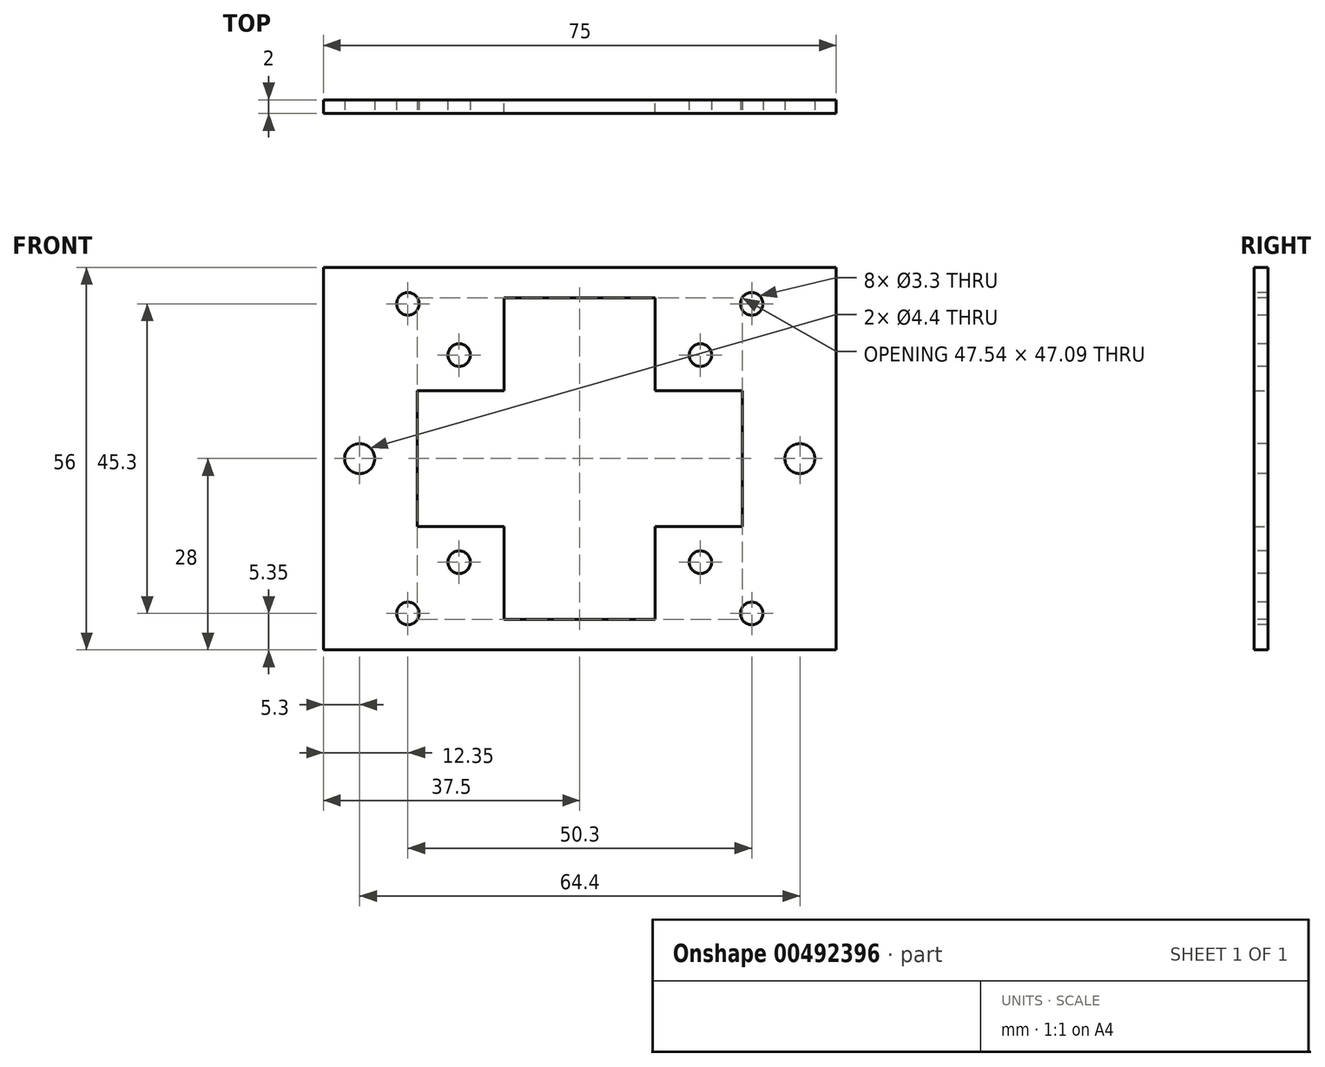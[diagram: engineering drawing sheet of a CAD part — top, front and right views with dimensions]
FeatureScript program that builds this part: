
annotation { "Feature Type Name" : "Feature", "Feature Type Description" : "" }
export const myFeature = defineFeature(function(context is Context, id is Id, definition is map)
    precondition{}
    {
        {
            var Q0;
            Q0=qCreatedBy(makeId("Front.planeOp"),FACE);
            var sketch = newSketch(context, id + "F0", { "sketchPlane" : qUnion([Q0])});
            skLineSegment(sketch, "E0.bottom", {"start": v(-37.5, 28) * mm, "end": v(37.5, 28) * mm});
            skLineSegment(sketch, "E0.top", {"start": v(-37.5, -28) * mm, "end": v(37.5, -28) * mm});
            skLineSegment(sketch, "E0.left", {"start": v(-37.5, 28) * mm, "end": v(-37.5, -28) * mm});
            skLineSegment(sketch, "E0.right", {"start": v(37.5, 28) * mm, "end": v(37.5, -28) * mm});
            skSolve(sketch);
        }
        {
            var Q0;
            Q0 = qSketchRegion(id + "F0", true);
            extrude(context, id + "F1", {"entities" : qUnion([Q0]), "depth" : 2 * mm, "offsetDistance" : 25 * mm});
        }
        {
            var Q0;
            Q0=makeQuery(id+"F1.opExtrude","CAP_FACE",FACE,{"disambiguationData":[OSD([sQuery(id+"F0.wireOp",EDGE,"E0.bottom"),sQuery(id+"F0.wireOp",EDGE,"E0.top"),sQuery(id+"F0.wireOp",EDGE,"E0.left"),sQuery(id+"F0.wireOp",EDGE,"E0.right")])],"isStart":false});
            var sketch = newSketch(context, id + "F2", { "sketchPlane" : qUnion([Q0])});
            skPoint(sketch, "E1", {"position": v(-32.2, 0) * mm});
            skPoint(sketch, "E2", {"position": v(32.2, 0) * mm});
            skSolve(sketch);
        }
        {
            var Q0;
            Q0=sQuery(id+"F2.wireOp",VERTEX,"E1");
            var Q1;
            Q1=sQuery(id+"F2.wireOp",VERTEX,"E2");
            var Q2;
            Q2=makeQuery(id+"F1.opExtrude","SWEPT_BODY",BODY,{"disambiguationData":[OSD([sQuery(id+"F0.wireOp",EDGE,"E0.bottom"),sQuery(id+"F0.wireOp",EDGE,"E0.top"),sQuery(id+"F0.wireOp",EDGE,"E0.left"),sQuery(id+"F0.wireOp",EDGE,"E0.right")])]});
            hole(context, id + "F3", {"style" : HoleStyle.SIMPLE, "endStyle" : HoleEndStyle.THROUGH, "standardTappedOrClearance" : lookupTablePath({ "standard" : "ISO", "fit" : "Normal", "size" : "M4", "type" : "Clearance" }), "standardBlindInLast" : lookupTablePath({ "fit" : "Standard", "standard" : "ISO", "size" : "M4", "type" : "Clearance" }), "holeDiameter" : 4.4 * mm, "majorDiameter" : 5 * mm, "isTappedThrough" : true, "tappedDepth" : 12 * mm, "tapClearance" : 3, "locations" : qUnion([Q0, Q1]), "scope" : qUnion([Q2])});
        }
        {
            var Q0;
            Q0=makeQuery(id+"F1.opExtrude","CAP_FACE",FACE,{"disambiguationData":[OSD([sQuery(id+"F0.wireOp",EDGE,"E0.bottom"),sQuery(id+"F0.wireOp",EDGE,"E0.top"),sQuery(id+"F0.wireOp",EDGE,"E0.left"),sQuery(id+"F0.wireOp",EDGE,"E0.right")])],"isStart":false});
            var sketch = newSketch(context, id + "F4", { "sketchPlane" : qUnion([Q0])});
            skPoint(sketch, "E3", {"position": v(-25.15, 22.65) * mm});
            skPoint(sketch, "E4", {"position": v(25.15, 22.65) * mm});
            skPoint(sketch, "E5", {"position": v(-25.15, -22.65) * mm});
            skPoint(sketch, "E6", {"position": v(25.15, -22.65) * mm});
            skSolve(sketch);
        }
        {
            var Q0;
            Q0=sQuery(id+"F4.wireOp",VERTEX,"E3");
            var Q1;
            Q1=sQuery(id+"F4.wireOp",VERTEX,"E5");
            var Q2;
            Q2=sQuery(id+"F4.wireOp",VERTEX,"E6");
            var Q3;
            Q3=sQuery(id+"F4.wireOp",VERTEX,"E4");
            var Q4;
            Q4=makeQuery(id+"F1.opExtrude","SWEPT_BODY",BODY,{"disambiguationData":[OSD([sQuery(id+"F0.wireOp",EDGE,"E0.bottom"),sQuery(id+"F0.wireOp",EDGE,"E0.top"),sQuery(id+"F0.wireOp",EDGE,"E0.left"),sQuery(id+"F0.wireOp",EDGE,"E0.right")])]});
            hole(context, id + "F5", {"style" : HoleStyle.SIMPLE, "endStyle" : HoleEndStyle.THROUGH, "standardTappedOrClearance" : lookupTablePath({ "standard" : "ISO", "fit" : "Normal", "size" : "M3", "type" : "Clearance" }), "standardBlindInLast" : lookupTablePath({ "fit" : "Standard", "standard" : "ISO", "size" : "M3", "type" : "Clearance" }), "holeDiameter" : 3.3 * mm, "majorDiameter" : 5 * mm, "isTappedThrough" : true, "tappedDepth" : 12 * mm, "tapClearance" : 3, "locations" : qUnion([Q0, Q1, Q2, Q3]), "scope" : qUnion([Q4])});
        }
        {
            var Q0;
            Q0=makeQuery(id+"F1.opExtrude","CAP_FACE",FACE,{"disambiguationData":[OSD([sQuery(id+"F0.wireOp",EDGE,"E0.bottom"),sQuery(id+"F0.wireOp",EDGE,"E0.top"),sQuery(id+"F0.wireOp",EDGE,"E0.left"),sQuery(id+"F0.wireOp",EDGE,"E0.right")])],"isStart":false});
            var sketch = newSketch(context, id + "F6", { "sketchPlane" : qUnion([Q0])});
            skPoint(sketch, "E7", {"position": v(-17.65, 15.15) * mm});
            skPoint(sketch, "E8", {"position": v(17.65, 15.15) * mm});
            skPoint(sketch, "E9", {"position": v(-17.65, -15.15) * mm});
            skPoint(sketch, "E10", {"position": v(17.65, -15.15) * mm});
            skSolve(sketch);
        }
        {
            var Q0;
            Q0=sQuery(id+"F6.wireOp",VERTEX,"E7");
            var Q1;
            Q1=sQuery(id+"F6.wireOp",VERTEX,"E9");
            var Q2;
            Q2=sQuery(id+"F6.wireOp",VERTEX,"E10");
            var Q3;
            Q3=sQuery(id+"F6.wireOp",VERTEX,"E8");
            var Q4;
            Q4=makeQuery(id+"F1.opExtrude","SWEPT_BODY",BODY,{"disambiguationData":[OSD([sQuery(id+"F0.wireOp",EDGE,"E0.bottom"),sQuery(id+"F0.wireOp",EDGE,"E0.top"),sQuery(id+"F0.wireOp",EDGE,"E0.left"),sQuery(id+"F0.wireOp",EDGE,"E0.right")])]});
            hole(context, id + "F7", {"style" : HoleStyle.SIMPLE, "endStyle" : HoleEndStyle.THROUGH, "standardTappedOrClearance" : lookupTablePath({ "standard" : "ISO", "fit" : "Normal", "size" : "M3", "type" : "Clearance" }), "standardBlindInLast" : lookupTablePath({ "fit" : "Standard", "standard" : "ISO", "size" : "M3", "type" : "Clearance" }), "holeDiameter" : 3.3 * mm, "majorDiameter" : 5 * mm, "isTappedThrough" : true, "tappedDepth" : 12 * mm, "tapClearance" : 3, "locations" : qUnion([Q0, Q1, Q2, Q3]), "scope" : qUnion([Q4])});
        }
        {
            var Q0;
            Q0=makeQuery(id+"F1.opExtrude","CAP_FACE",FACE,{"disambiguationData":[OSD([sQuery(id+"F0.wireOp",EDGE,"E0.bottom"),sQuery(id+"F0.wireOp",EDGE,"E0.top"),sQuery(id+"F0.wireOp",EDGE,"E0.left"),sQuery(id+"F0.wireOp",EDGE,"E0.right")])],"isStart":false});
            var sketch = newSketch(context, id + "F8", { "sketchPlane" : qUnion([Q0])});
            skLineSegment(sketch, "E11.bottom", {"start": v(-23.77, 9.96) * mm, "end": v(23.77, 9.96) * mm});
            skLineSegment(sketch, "E11.top", {"start": v(-23.77, -9.96) * mm, "end": v(23.77, -9.96) * mm});
            skLineSegment(sketch, "E11.left", {"start": v(-23.77, 9.96) * mm, "end": v(-23.77, -9.96) * mm});
            skLineSegment(sketch, "E11.right", {"start": v(23.77, 9.96) * mm, "end": v(23.77, -9.96) * mm});
            skPoint(sketch, "E11.middle", {"position": v(0, 0) * mm});
            skSolve(sketch);
        }
        {
            var Q0;
            Q0=makeQuery(id+"F8.imprint","IMPRINT",FACE,{"disambiguationData":[TD([[makeQuery(id+"F8.imprint","IMPRINT",EDGE,{"derivedFrom":sQuery(id+"F8.wireOp",EDGE,"E11.bottom")}),-1.0]])]});
            extrude(context, id + "F9", {"entities" : qUnion([Q0]), "operationType" : NewBodyOperationType.REMOVE, "oppositeDirection" : true, "depth" : 25 * mm, "offsetDistance" : 25 * mm});
        }
        {
            var Q0;
            Q0=makeQuery(id+"F1.opExtrude","CAP_FACE",FACE,{"disambiguationData":[OSD([sQuery(id+"F0.wireOp",EDGE,"E0.bottom"),sQuery(id+"F0.wireOp",EDGE,"E0.top"),sQuery(id+"F0.wireOp",EDGE,"E0.left"),sQuery(id+"F0.wireOp",EDGE,"E0.right")])],"isStart":false});
            var sketch = newSketch(context, id + "F10", { "sketchPlane" : qUnion([Q0])});
            skLineSegment(sketch, "E12.bottom", {"start": v(-11.05, 23.55) * mm, "end": v(11.05, 23.55) * mm});
            skLineSegment(sketch, "E12.top", {"start": v(-11.05, -23.55) * mm, "end": v(11.05, -23.55) * mm});
            skLineSegment(sketch, "E12.left", {"start": v(-11.05, 23.55) * mm, "end": v(-11.05, -23.55) * mm});
            skLineSegment(sketch, "E12.right", {"start": v(11.05, 23.55) * mm, "end": v(11.05, -23.55) * mm});
            skPoint(sketch, "E12.middle", {"position": v(0, 0) * mm});
            skSolve(sketch);
        }
        {
            var Q0;
            Q0 = qSketchRegion(id + "F10", true);
            extrude(context, id + "F11", {"entities" : qUnion([Q0]), "operationType" : NewBodyOperationType.REMOVE, "oppositeDirection" : true, "depth" : 25 * mm, "offsetDistance" : 25 * mm});
        }
    });
